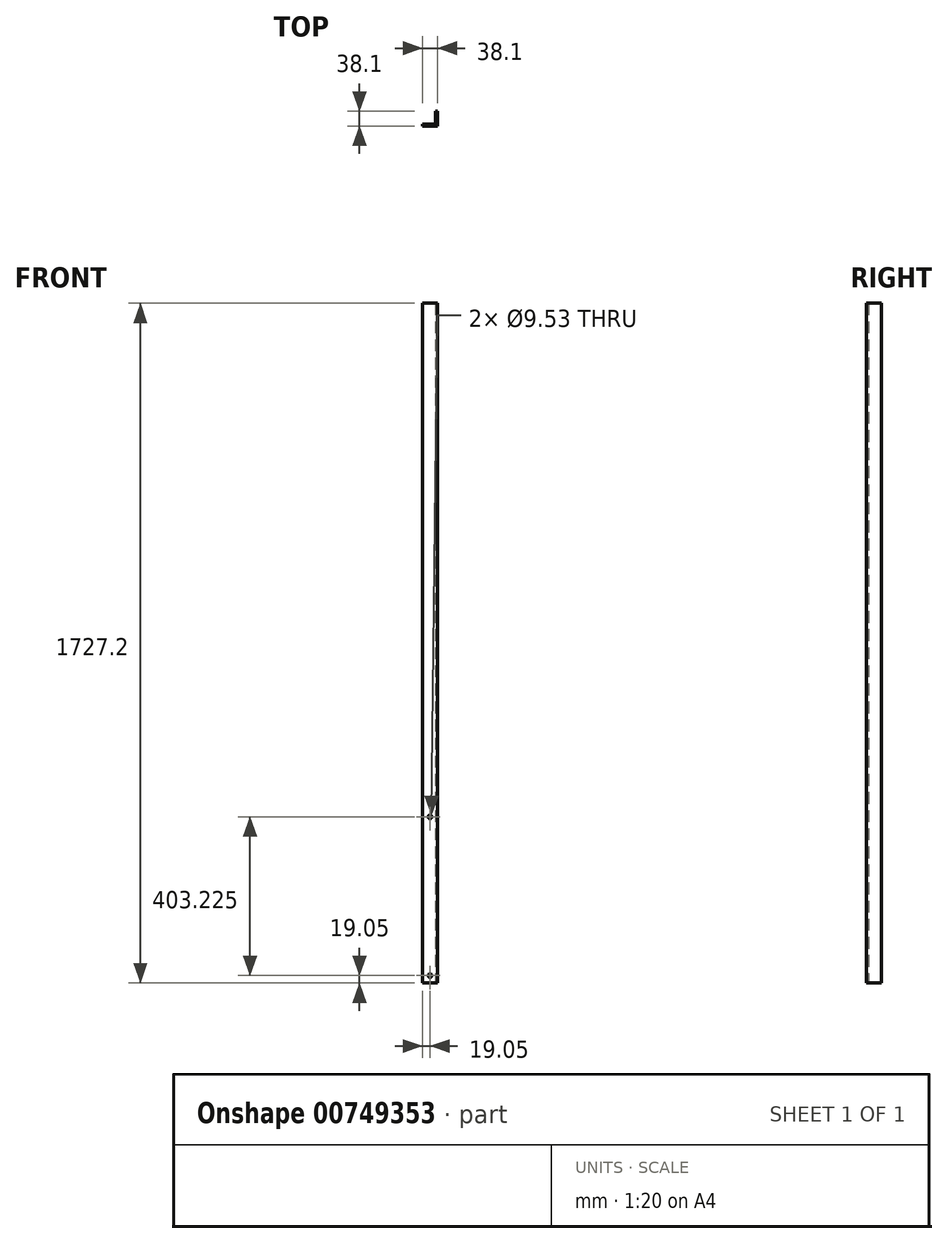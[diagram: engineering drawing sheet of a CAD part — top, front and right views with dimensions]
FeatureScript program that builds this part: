
annotation { "Feature Type Name" : "Feature", "Feature Type Description" : "" }
export const myFeature = defineFeature(function(context is Context, id is Id, definition is map)
    precondition{}
    {
        {
            var Q0;
            Q0=qCreatedBy(makeId("Top.planeOp"),FACE);
            var sketch = newSketch(context, id + "F0", { "sketchPlane" : qUnion([Q0])});
            skLineSegment(sketch, "E0", {"start": v(0, 0) * mm, "end": v(38.1, 0) * mm});
            skLineSegment(sketch, "E1", {"start": v(38.1, 0) * mm, "end": v(38.1, 38.1) * mm});
            skLineSegment(sketch, "E2", {"start": v(38.1, 38.1) * mm, "end": v(33.34, 38.1) * mm});
            skLineSegment(sketch, "E3", {"start": v(33.34, 38.1) * mm, "end": v(33.34, 4.76) * mm});
            skLineSegment(sketch, "E4", {"start": v(33.34, 4.76) * mm, "end": v(0, 4.76) * mm});
            skLineSegment(sketch, "E5", {"start": v(0, 4.76) * mm, "end": v(0, 0) * mm});
            skSolve(sketch);
        }
        {
            var Q0;
            Q0=makeQuery(id+"F0.imprint","IMPRINT",FACE,{"disambiguationData":[TD([[makeQuery(id+"F0.imprint","IMPRINT",EDGE,{"derivedFrom":sQuery(id+"F0.wireOp",EDGE,"E0")}),1.0]])]});
            extrude(context, id + "F1", {"entities" : qUnion([Q0]), "depth" : 1727.2 * mm, "offsetDistance" : 25.4 * mm});
        }
        {
            var Q0;
            Q0=makeQuery(id+"F1.opExtrude","SWEPT_FACE",FACE,{"disambiguationData":[OSD([sQuery(id+"F0.wireOp",EDGE,"E0")])]});
            var sketch = newSketch(context, id + "F2", { "sketchPlane" : qUnion([Q0])});
            skCircle(sketch, "E6", {"center": v(19.05, 19.05) * mm, "radius": 4.76 * mm});
            skSolve(sketch);
        }
        {
            var Q0;
            Q0=makeQuery(id+"F2.imprint","IMPRINT",FACE,{"disambiguationData":[TD([[makeQuery(id+"F2.imprint","IMPRINT",EDGE,{"derivedFrom":sQuery(id+"F2.wireOp",EDGE,"E6")}),1.0]])]});
            extrude(context, id + "F3", {"entities" : qUnion([Q0]), "operationType" : NewBodyOperationType.REMOVE, "endBound" : BoundingType.THROUGH_ALL, "oppositeDirection" : true, "depth" : 25.4 * mm, "offsetDistance" : 25.4 * mm});
        }
        {
            var Q0;
            Q0=makeQuery(id+"F1.opExtrude","SWEPT_FACE",FACE,{"disambiguationData":[OSD([sQuery(id+"F0.wireOp",EDGE,"E0")])]});
            var sketch = newSketch(context, id + "F4", { "sketchPlane" : qUnion([Q0])});
            skCircle(sketch, "E7", {"center": v(19.05, 422.28) * mm, "radius": 4.76 * mm});
            skCircle(sketch, "E8.0", {"center": v(19.05, 19.05) * mm, "radius": 4.76 * mm});
            skSolve(sketch);
        }
        {
            var Q0;
            Q0=makeQuery(id+"F4.imprint","IMPRINT",FACE,{"disambiguationData":[TD([[makeQuery(id+"F4.imprint","IMPRINT",EDGE,{"derivedFrom":sQuery(id+"F4.wireOp",EDGE,"E7")}),1.0]])]});
            extrude(context, id + "F5", {"entities" : qUnion([Q0]), "operationType" : NewBodyOperationType.REMOVE, "endBound" : BoundingType.THROUGH_ALL, "oppositeDirection" : true, "depth" : 25.4 * mm, "offsetDistance" : 25.4 * mm});
        }
    });
